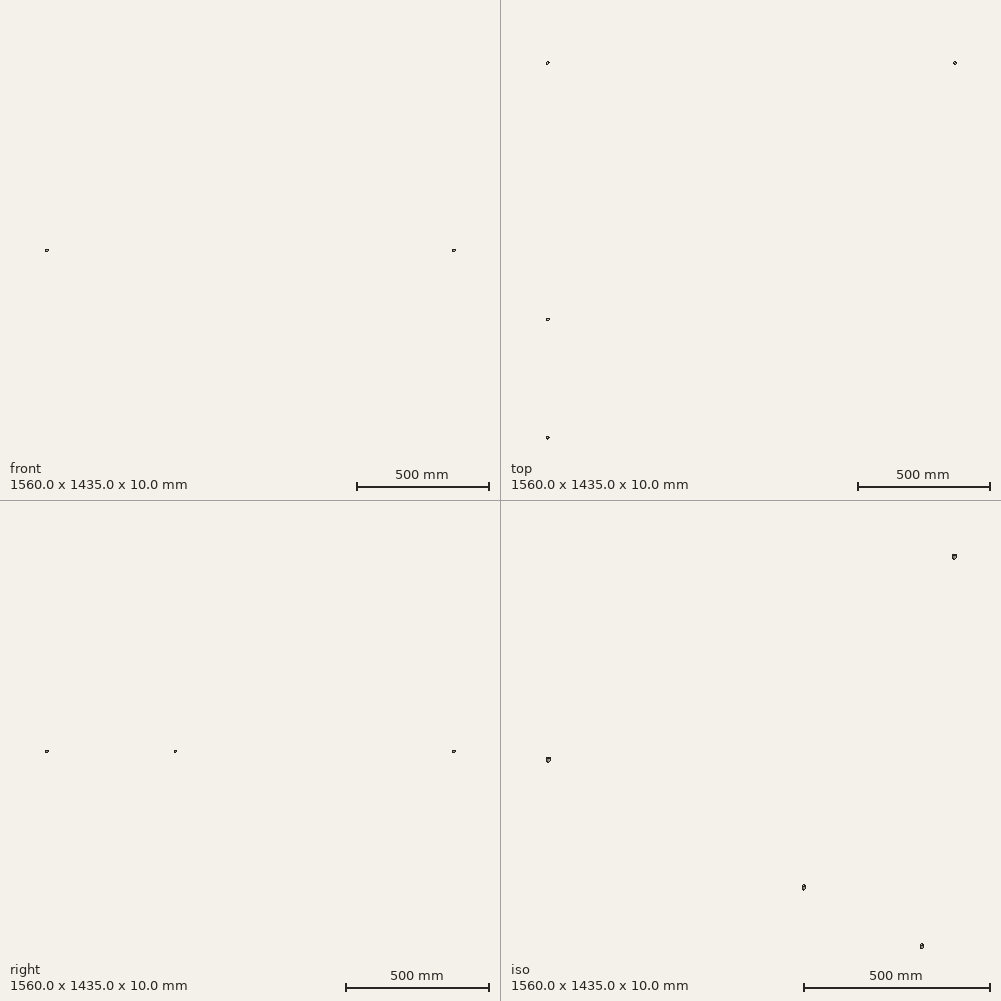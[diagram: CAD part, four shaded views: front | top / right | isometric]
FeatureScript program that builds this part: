
annotation { "Feature Type Name" : "Feature", "Feature Type Description" : "" }
export const myFeature = defineFeature(function(context is Context, id is Id, definition is map)
    precondition{}
    {
        {
            var Q0;
            Q0=qCreatedBy(makeId("Top.planeOp"),FACE);
            var sketch = newSketch(context, id + "F0", { "sketchPlane" : qUnion([Q0])});
            skLineSegment(sketch, "E0", {"start": v(0, 0) * mm, "end": v(0, 450) * mm});
            skCircle(sketch, "E1", {"center": v(0, 0) * mm, "radius": 5 * mm});
            skCircle(sketch, "E2", {"center": v(0, 450) * mm, "radius": 5 * mm});
            skLineSegment(sketch, "E3", {"start": v(0, 0) * mm, "end": v(0, 1425) * mm});
            skCircle(sketch, "E4", {"center": v(0, 1425) * mm, "radius": 5 * mm});
            skLineSegment(sketch, "E5", {"start": v(0, 0) * mm, "end": v(1550, 0) * mm});
            skLineSegment(sketch, "E6", {"start": v(1550, 0) * mm, "end": v(1550, 1425) * mm});
            skCircle(sketch, "E7", {"center": v(1550, 1425) * mm, "radius": 5 * mm});
            skSolve(sketch);
        }
        {
            var Q0;
            Q0 = qSketchRegion(id + "F0", true);
            extrude(context, id + "F1", {"entities" : qUnion([Q0]), "depth" : 10 * mm, "offsetDistance" : 25 * mm});
        }
    });
